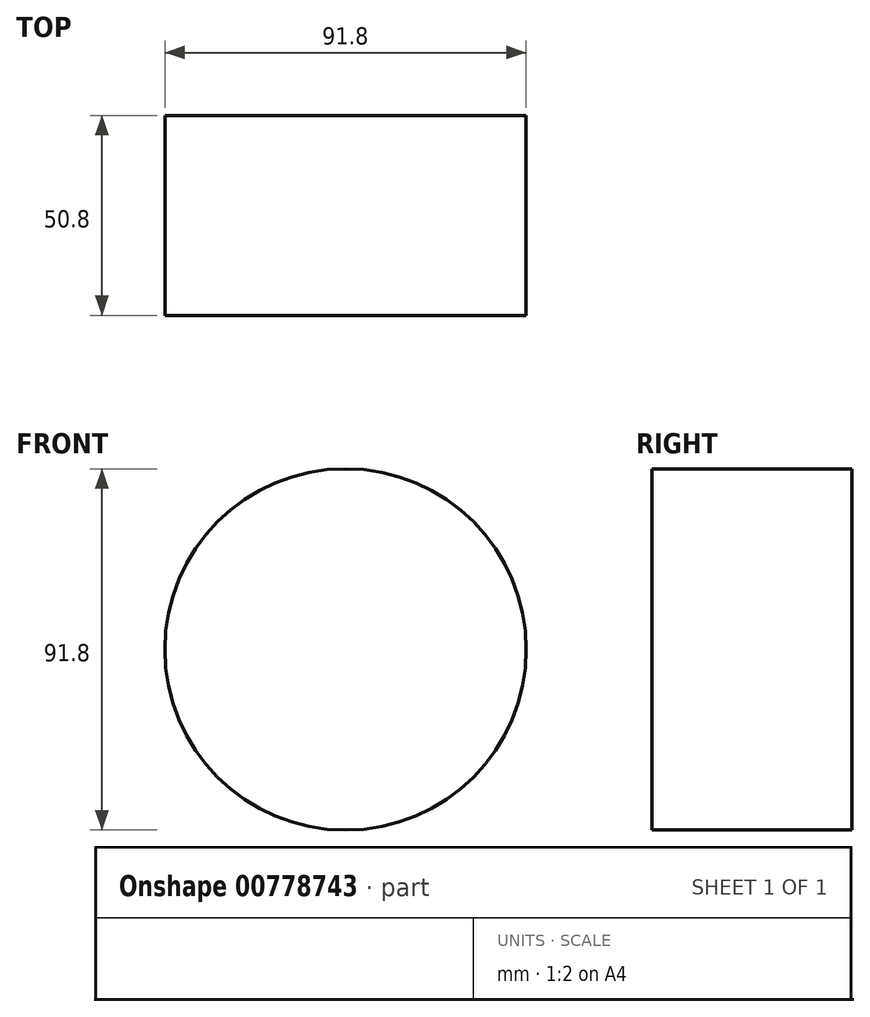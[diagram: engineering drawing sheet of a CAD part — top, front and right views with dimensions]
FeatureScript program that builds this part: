
annotation { "Feature Type Name" : "Feature", "Feature Type Description" : "" }
export const myFeature = defineFeature(function(context is Context, id is Id, definition is map)
    precondition{}
    {
        {
            var Q0;
            Q0=qCreatedBy(makeId("Front.planeOp"),FACE);
            var sketch = newSketch(context, id + "F0", { "sketchPlane" : qUnion([Q0])});
            skCircle(sketch, "E0", {"center": v(0, 0) * mm, "radius": 45.9 * mm});
            skSolve(sketch);
        }
        {
            var Q0;
            Q0 = qSketchRegion(id + "F0", true);
            extrude(context, id + "F1", {"entities" : qUnion([Q0]), "depth" : 50.8 * mm, "offsetDistance" : 25.4 * mm});
        }
    });
